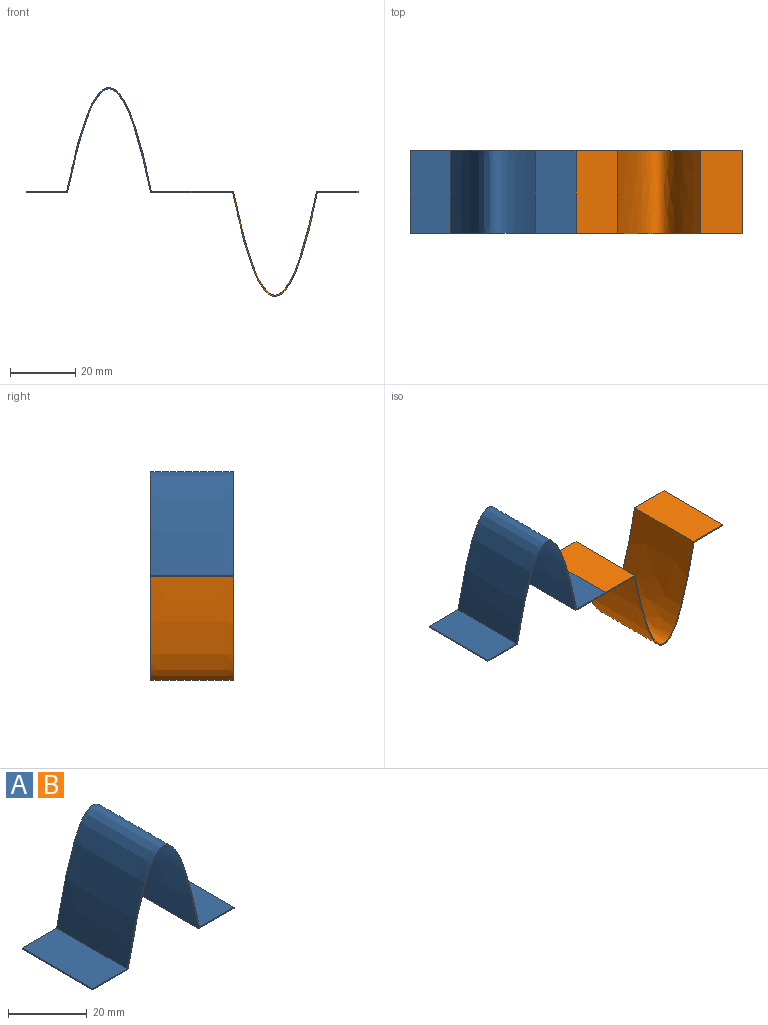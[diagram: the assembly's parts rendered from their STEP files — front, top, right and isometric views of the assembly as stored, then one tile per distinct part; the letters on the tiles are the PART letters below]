
ASSEMBLY  parts=2 mates=1
PART A: 10 faces, bbox 50.8x25.4x43.7 mm
  f0: extruded ~31.75x25.4mm, area 1794mm2, adj f1,f7,f8,f9
  f1: plane 25.4x12.7mm, normal (0,0,-1), area 322.6mm2, adj f0,f2,f8,f9
  f2: plane 25.4x0.36mm, normal (1,0,0), area 9mm2, adj f1,f3,f8,f9
  f3: plane 25.4x12.41mm, normal (0,0,1), area 315.2mm2, adj f2,f4,f8,f9
  f4: extruded ~31.75x25.98mm, area 1804mm2, adj f3,f5,f8,f9
  f5: plane 25.4x12.41mm, normal (0,0,1), area 315.2mm2, adj f4,f6,f8,f9
  f6: plane 25.4x0.36mm, normal (-1,0,0), area 9mm2, adj f5,f7,f8,f9
  f7: plane 25.4x12.7mm, normal (0,0,-1), area 322.6mm2, adj f0,f6,f8,f9
  f8: plane 50.8x43.66mm, normal (0,-1,0), area 34.1mm2, adj f0,f1,f2,f3,f4,f5,f6,f7
  f9: plane 50.8x43.66mm, normal (0,1,0), area 34.1mm2, adj f0,f1,f2,f3,f4,f5,f6,f7
PART B: same geometry as A
PLACE A at identity fixed
PLACE B rot(axis=(1,0,0),180deg) t=(50.8,-25.4,0.36)mm
MATE fastened A.f2 <-> B.f6  axis (1,0,0) through (0,-12.7,0.18)mm
